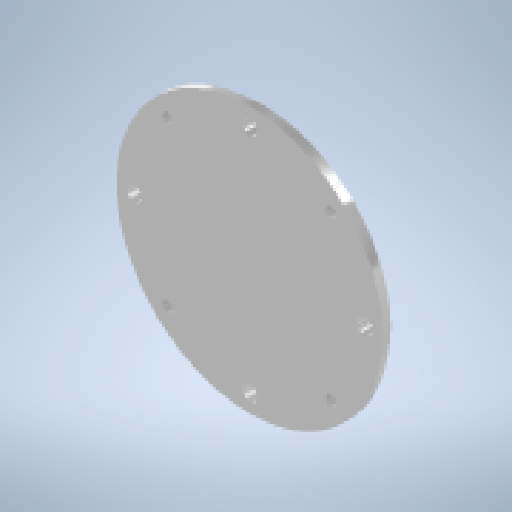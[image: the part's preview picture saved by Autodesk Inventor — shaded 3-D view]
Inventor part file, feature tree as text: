
AUTODESK INVENTOR PART (.ipt)
format: ipt  version: 2024 (Build 280153000, 153)  size: 177,664 bytes
history: native  units: mm
features: sketch x5, extrude x3, hole x2, pattern_circular x2, other x1, thread x1
ambient origin geometry x8: Origin, YZ Plane, XZ Plane, XY Plane, X Axis, Y Axis, Z Axis, Center Point
bodies: Body1 (feature_tree)
feature tree (14):
  other  "ソリッド1"
  extrude  "押し出し1"  Depth=100.0mm
  extrude  "押し出し2"  Depth=2.5mm TaperAngle=0.0deg
  hole  "穴1"  [1 undecoded]
  pattern_circular  "円形状パターン1"  [2 undecoded]
  hole  "穴2"  [1 undecoded]
  thread  "ねじ1"
  pattern_circular  "円形状パターン2"  Count=4 Angle=360.0deg
  extrude  "押し出し3"  TaperAngle=45.0deg  [1 undecoded]
  sketch  "スケッチ1"
  sketch  "スケッチ2"
  sketch  "スケッチ3"
  sketch  "スケッチ4"
  sketch  "スケッチ5"
note: 5 required parameter values undecoded (feature->parameter linkage not recoverable at this tier; creation-order binding heuristic only, values carry confidence <= 0.55)
